# Revit family: Mirror-RotatingMirror-35cm-Vitra-PluralSeries-65852
name_source: partatom
category: Furniture Systems
revit_build: Autodesk Revit 2017 (Build: 20160225_1515(x64)
units: mm (PartAtom-declared; Revit-internal decimal feet)

## family parameters
Cut with Voids When Loaded = No
Host = Face
OmniClass Number = 23.40.00.00
OmniClass Title = Equipment and Furnishings
Part Type = Normal
Room Calculation Point = No
Round Connector Dimension = Use Diameter
Shared = Yes

## types (2) — shared parameters
BIMobject category = Mirrors
Brand = VitrA
Default Elevation = 1200 mm
Design country = Turkey
IFC Classification = Furniture
Main Material = Glass
Manufacturer = VitrA
Manufacturer name = VitrA
Masterformat 2014 Code = 08 83 00
Masterformat 2014 Description = Mirrors
Mounting type = Wall-Hung
Nominal Depth (mm) = 250 mm
Nominal Height (mm) = 900 mm  [stored 2.95276 ft]
Nominal Width (mm) = 380 mm  [stored 1.24672 ft]
OmniClass Code = 23-21 00 00
OmniClass Description = Furnishings, Fixtures and Equipment Products
Primary Material = Mirror
Product certification = https://www.vitraglobal.com
Product family = Plural
Product group = Mirror
Third Material = Metal
UNSPSC Code = 56
UNSPSC Description = Mirrors
URL = https://vitraglobal.com
Uniclass 1.4 Code = L8732
Uniclass 1.4 Description = Mirrors
Uniclass 2.0 Code = PR-71-55
Uniclass 2.0 Description = Mirrors
Uniclass 2015 Code = Pr_25_71_53
Uniclass 2015 Name = Mirrors
Uniformat II Code = E20
Uniformat II Description = FURNISHINGS
Warranty Period (Year) = 2
Weight Net (kg) = 10,500
Youtube = https://www.youtube.com

## per-type parameters (varying)
| type | Article No. (default) | Color | Description | Model | Product SKU | Product data url | Product url | Secondary Material | Technical description |
| Mirror-RotatingMirror-Vitra-Plural_65852 | 65852 | Black Oak | Plural Rotating Mirror - 35cm - Black Oak | 65852 | 65852 |  | https://www.vitraglobal.com | Black Oak | https://www.vitraglobal.com |
| Mirror-RotatingMirror-Vitra-Plural_64059 | 64059 | Dark Oak | Plural Rotating Mirror - 35cm - Dark Oak | 64059 | 64059 | https://www.bimobject.com | https://www.vitra.com.tr | Dark Oak | https://www.vitra.com.tr |

note: [stored X ft] marks values corroborated as IEEE doubles in the binary element streams (Revit-internal decimal feet)

## geometry (parser evidence)
native form markers: Sweep x2
no freeform markers — native parametric forms only
